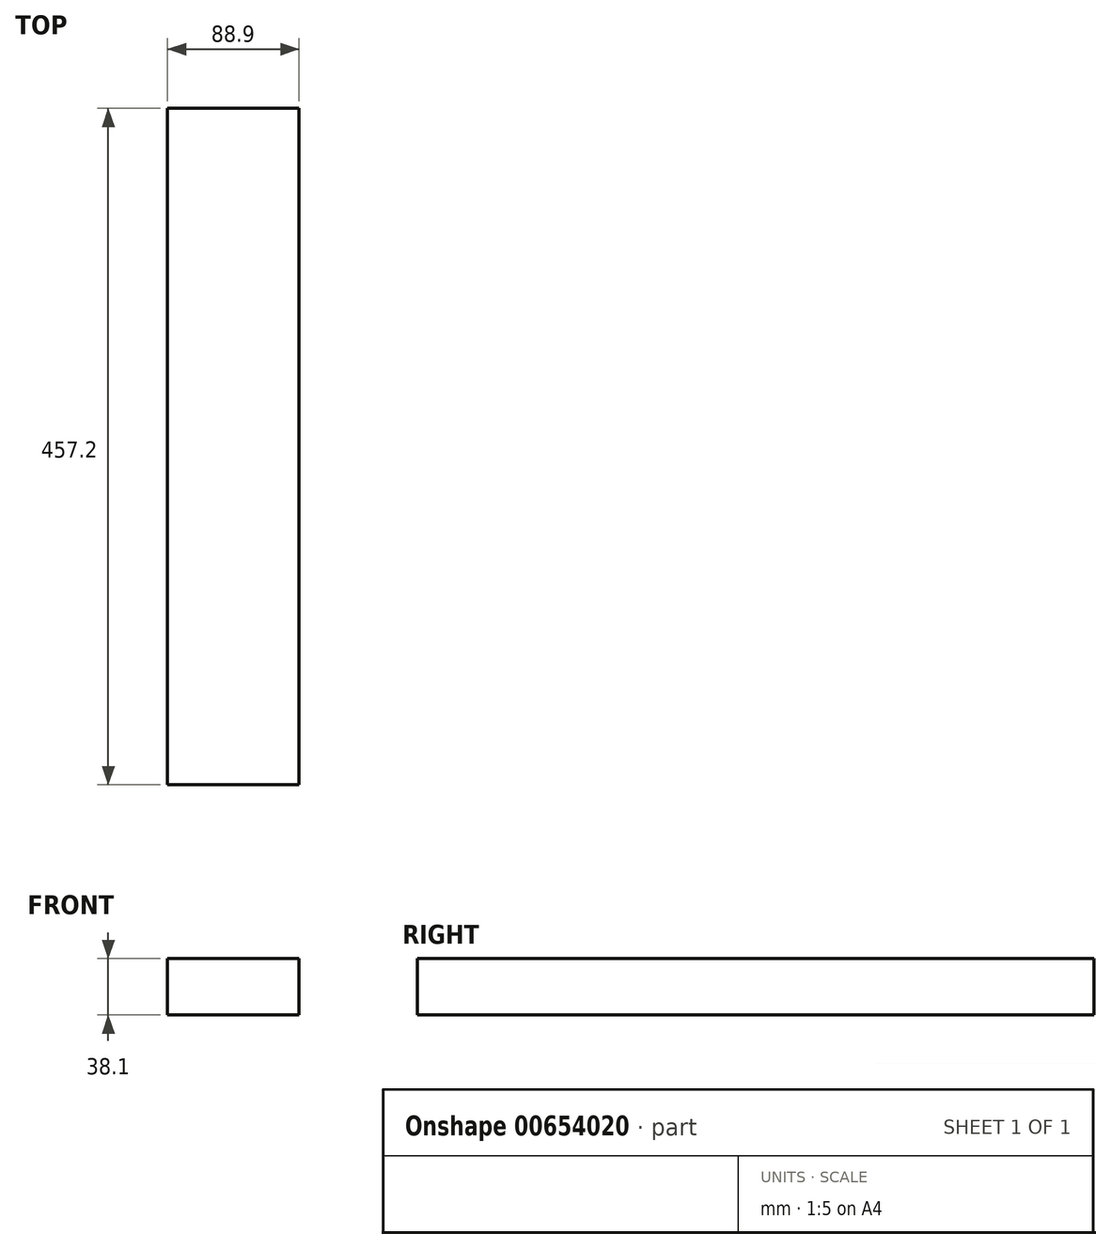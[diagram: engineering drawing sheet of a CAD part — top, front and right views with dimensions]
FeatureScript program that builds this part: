
annotation { "Feature Type Name" : "Feature", "Feature Type Description" : "" }
export const myFeature = defineFeature(function(context is Context, id is Id, definition is map)
    precondition{}
    {
        {
            var Q0;
            Q0=qCreatedBy(makeId("Front.planeOp"),FACE);
            var sketch = newSketch(context, id + "F0", { "sketchPlane" : qUnion([Q0])});
            skLineSegment(sketch, "E0.bottom", {"start": v(0, 0) * mm, "end": v(88.9, 0) * mm});
            skLineSegment(sketch, "E0.top", {"start": v(0, 38.1) * mm, "end": v(88.9, 38.1) * mm});
            skLineSegment(sketch, "E0.left", {"start": v(0, 0) * mm, "end": v(0, 38.1) * mm});
            skLineSegment(sketch, "E0.right", {"start": v(88.9, 0) * mm, "end": v(88.9, 38.1) * mm});
            skSolve(sketch);
        }
        {
            var Q0;
            Q0=makeQuery(id+"F0.imprint","IMPRINT",FACE,{"disambiguationData":[TD([[makeQuery(id+"F0.imprint","IMPRINT",EDGE,{"derivedFrom":sQuery(id+"F0.wireOp",EDGE,"E0.bottom")}),1.0]])]});
            extrude(context, id + "F1", {"entities" : qUnion([Q0]), "depth" : 457.2 * mm, "offsetDistance" : 25.4 * mm});
        }
    });
